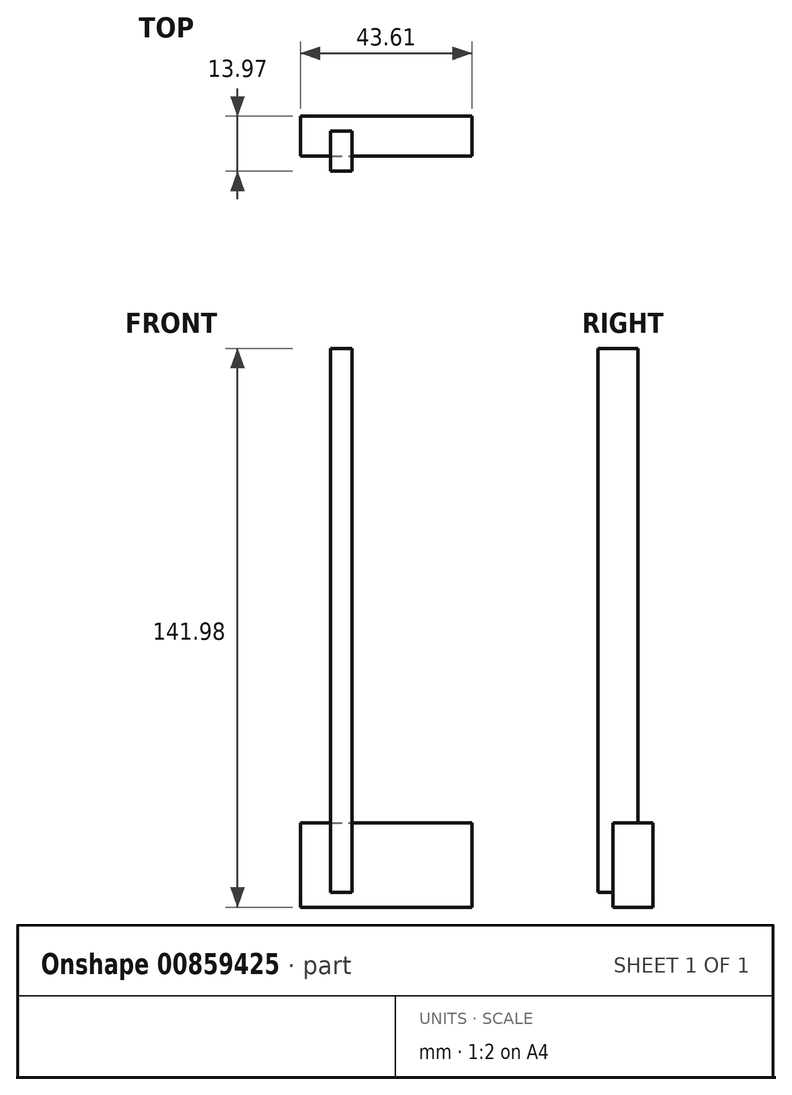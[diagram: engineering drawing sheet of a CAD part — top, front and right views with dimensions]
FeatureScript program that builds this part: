
annotation { "Feature Type Name" : "Feature", "Feature Type Description" : "" }
export const myFeature = defineFeature(function(context is Context, id is Id, definition is map)
    precondition{}
    {
        {
            var Q0;
            Q0=qCreatedBy(makeId("Front.planeOp"),FACE);
            var sketch = newSketch(context, id + "F0", { "sketchPlane" : qUnion([Q0])});
            skLineSegment(sketch, "E0.bottom", {"start": v(-108.44, 51.07) * mm, "end": v(-102.9, 51.07) * mm});
            skLineSegment(sketch, "E0.top", {"start": v(-108.44, -87.11) * mm, "end": v(-102.9, -87.11) * mm});
            skLineSegment(sketch, "E0.left", {"start": v(-108.44, 51.07) * mm, "end": v(-108.44, -87.11) * mm});
            skLineSegment(sketch, "E0.right", {"start": v(-102.9, 51.07) * mm, "end": v(-102.9, -87.11) * mm});
            skSolve(sketch);
        }
        {
            var Q0;
            Q0=makeQuery(id+"F0.imprint","IMPRINT",FACE,{"disambiguationData":[TD([[makeQuery(id+"F0.imprint","IMPRINT",EDGE,{"derivedFrom":sQuery(id+"F0.wireOp",EDGE,"E0.bottom")}),-1.0]])]});
            extrude(context, id + "F1", {"entities" : qUnion([Q0]), "depth" : 3.8 * mm, "offsetDistance" : 25.4 * mm});
        }
        {
            var Q0;
            Q0=qCreatedBy(makeId("Front.planeOp"),FACE);
            var sketch = newSketch(context, id + "F2", { "sketchPlane" : qUnion([Q0])});
            skLineSegment(sketch, "E1.bottom", {"start": v(-116.03, -90.9) * mm, "end": v(-72.42, -90.9) * mm});
            skLineSegment(sketch, "E1.top", {"start": v(-116.03, -69.44) * mm, "end": v(-72.42, -69.44) * mm});
            skLineSegment(sketch, "E1.left", {"start": v(-116.03, -90.9) * mm, "end": v(-116.03, -69.44) * mm});
            skLineSegment(sketch, "E1.right", {"start": v(-72.42, -90.9) * mm, "end": v(-72.42, -69.44) * mm});
            skSolve(sketch);
        }
        {
            var Q0;
            Q0 = qSketchRegion(id + "F2", true);
            var Q1;
            Q1=makeQuery(id+"F1.opExtrude","CAP_FACE",FACE,{"disambiguationData":[OSD([sQuery(id+"F0.wireOp",EDGE,"E0.bottom"),sQuery(id+"F0.wireOp",EDGE,"E0.top"),sQuery(id+"F0.wireOp",EDGE,"E0.left"),sQuery(id+"F0.wireOp",EDGE,"E0.right")])],"isStart":false});
            extrude(context, id + "F3", {"entities" : qUnion([Q0, Q1]), "operationType" : NewBodyOperationType.ADD, "oppositeDirection" : true, "depth" : 10.16 * mm, "offsetDistance" : 25.4 * mm});
        }
    });
